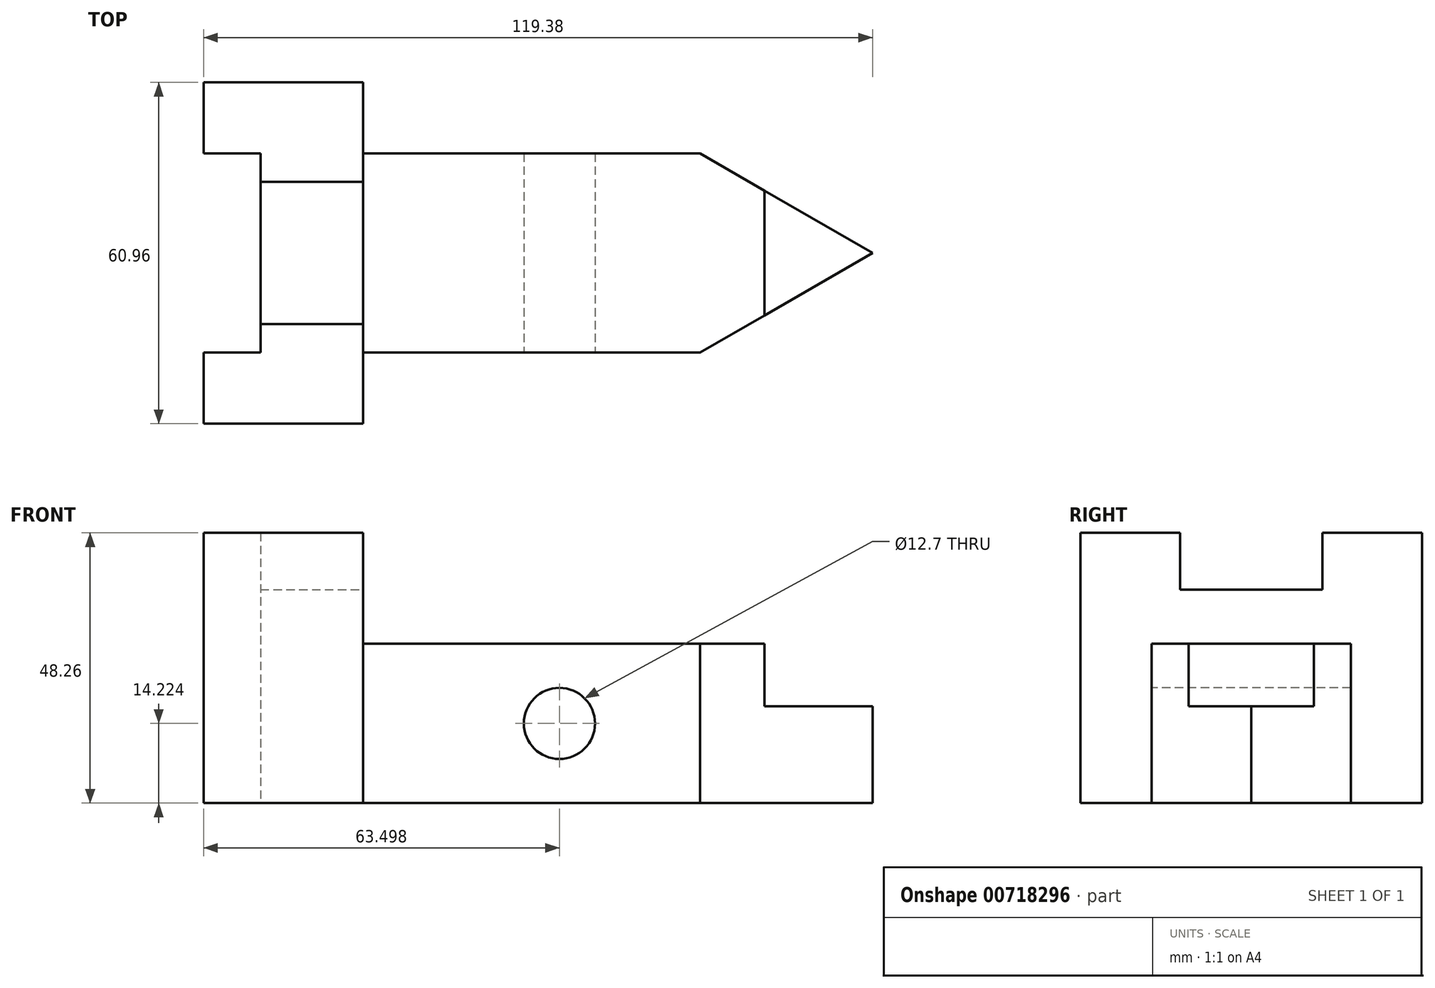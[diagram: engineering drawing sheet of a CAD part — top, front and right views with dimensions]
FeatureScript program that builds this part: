
annotation { "Feature Type Name" : "Feature", "Feature Type Description" : "" }
export const myFeature = defineFeature(function(context is Context, id is Id, definition is map)
    precondition{}
    {
        {
            var Q0;
            Q0=qCreatedBy(makeId("Top.planeOp"),FACE);
            var sketch = newSketch(context, id + "F0", { "sketchPlane" : qUnion([Q0])});
            skLineSegment(sketch, "E0.bottom", {"start": v(-46.91, 38.47) * mm, "end": v(-18.46, 38.47) * mm});
            skLineSegment(sketch, "E0.top", {"start": v(-46.91, -22.49) * mm, "end": v(-18.46, -22.49) * mm});
            skLineSegment(sketch, "E0.left", {"start": v(-46.91, 38.47) * mm, "end": v(-46.91, 25.77) * mm});
            skLineSegment(sketch, "E1", {"start": v(-18.46, 38.47) * mm, "end": v(-18.46, -22.49) * mm});
            skLineSegment(sketch, "E2", {"start": v(-18.46, -9.79) * mm, "end": v(41.67, -9.79) * mm});
            skLineSegment(sketch, "E3", {"start": v(-18.46, 25.77) * mm, "end": v(41.67, 25.77) * mm});
            skLineSegment(sketch, "E4", {"start": v(-46.91, -9.79) * mm, "end": v(-36.75, -9.79) * mm});
            skLineSegment(sketch, "E5", {"start": v(-36.75, -9.79) * mm, "end": v(-36.75, -4.7) * mm});
            skLineSegment(sketch, "E6", {"start": v(-36.75, -4.7) * mm, "end": v(-18.46, -4.7) * mm});
            skLineSegment(sketch, "E7", {"start": v(-46.91, 25.77) * mm, "end": v(-36.75, 25.77) * mm});
            skLineSegment(sketch, "E8", {"start": v(-36.75, 25.77) * mm, "end": v(-36.75, 20.7) * mm});
            skLineSegment(sketch, "E9", {"start": v(-36.75, 20.7) * mm, "end": v(-18.46, 20.7) * mm});
            skLineSegment(sketch, "E10", {"start": v(-36.75, 20.7) * mm, "end": v(-36.75, -4.7) * mm});
            skLineSegment(sketch, "E11", {"start": v(72.47, 8) * mm, "end": v(41.67, 25.77) * mm});
            skLineSegment(sketch, "E12", {"start": v(72.47, 8) * mm, "end": v(41.67, -9.79) * mm});
            skLineSegment(sketch, "E13.trimOffspring", {"start": v(53.16, 19.14) * mm, "end": v(53.16, -3.15) * mm});
            skLineSegment(sketch, "E14.trimOffspring", {"start": v(-46.91, -9.79) * mm, "end": v(-46.91, -22.49) * mm});
            skSolve(sketch);
        }
        {
            var Q0;
            {var subQ0=sQuery(id+"F0.wireOp",EDGE,"E2");Q0=makeQuery(id+"F0.imprint","IMPRINT",FACE,{"disambiguationData":[TD([[makeQuery(id+"F0.imprint","IMPRINT",EDGE,{"derivedFrom":subQ0}),1.0]])]});}
            extrude(context, id + "F1", {"entities" : qUnion([Q0]), "depth" : 28.45 * mm, "offsetDistance" : 25.4 * mm});
        }
        {
            var Q0;
            {var subQ3=sQuery(id+"F0.wireOp",EDGE,"E13.trimOffspring");Q0=makeQuery(id+"F0.imprint","IMPRINT",FACE,{"disambiguationData":[TD([[makeQuery(id+"F0.imprint","IMPRINT",EDGE,{"derivedFrom":subQ3}),1.0]])]});}
            extrude(context, id + "F2", {"entities" : qUnion([Q0]), "operationType" : NewBodyOperationType.ADD, "depth" : 17.27 * mm, "offsetDistance" : 25.4 * mm});
        }
        {
            var Q0;
            {var subQ3=sQuery(id+"F0.wireOp",EDGE,"E0.bottom");Q0=makeQuery(id+"F0.imprint","IMPRINT",FACE,{"disambiguationData":[TD([[makeQuery(id+"F0.imprint","IMPRINT",EDGE,{"derivedFrom":subQ3}),-1.0]])]});}
            var Q1;
            {var subQ1=sQuery(id+"F0.wireOp",EDGE,"E0.top");Q1=makeQuery(id+"F0.imprint","IMPRINT",FACE,{"disambiguationData":[TD([[makeQuery(id+"F0.imprint","IMPRINT",EDGE,{"derivedFrom":subQ1}),1.0]])]});}
            extrude(context, id + "F3", {"entities" : qUnion([Q0, Q1]), "operationType" : NewBodyOperationType.ADD, "depth" : 48.26 * mm, "offsetDistance" : 25.4 * mm});
        }
        {
            var Q0;
            {var subQ0=sQuery(id+"F0.wireOp",EDGE,"E6");Q0=makeQuery(id+"F0.imprint","IMPRINT",FACE,{"disambiguationData":[TD([[makeQuery(id+"F0.imprint","IMPRINT",EDGE,{"derivedFrom":subQ0}),1.0]])]});}
            extrude(context, id + "F4", {"entities" : qUnion([Q0]), "operationType" : NewBodyOperationType.ADD, "depth" : 38.1 * mm, "offsetDistance" : 25.4 * mm});
        }
        {
            var Q0;
            Q0=makeQuery(id+"F1.opExtrude","SWEPT_FACE",FACE,{"disambiguationData":[OSD([sQuery(id+"F0.wireOp",EDGE,"E2")])]});
            var sketch = newSketch(context, id + "F5", { "sketchPlane" : qUnion([Q0])});
            skCircle(sketch, "E15", {"center": v(16.59, 14.22) * mm, "radius": 6.35 * mm});
            skSolve(sketch);
        }
        {
            var Q0;
            Q0=makeQuery(id+"F5.imprint","IMPRINT",FACE,{"disambiguationData":[TD([[makeQuery(id+"F5.imprint","IMPRINT",EDGE,{"derivedFrom":sQuery(id+"F5.wireOp",EDGE,"E15")}),1.0]])]});
            extrude(context, id + "F6", {"entities" : qUnion([Q0]), "operationType" : NewBodyOperationType.REMOVE, "oppositeDirection" : true, "depth" : 53.34 * mm, "offsetDistance" : 25.4 * mm});
        }
    });
